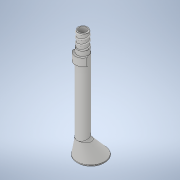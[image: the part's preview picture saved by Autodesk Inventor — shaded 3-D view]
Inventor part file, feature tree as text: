
AUTODESK INVENTOR PART (.ipt)
format: ipt  version: 2020 (Build 240168000, 168)  size: 341,504 bytes
history: native  units: mm
features: sketch x11, extrude x7, plane x5, fillet x4, other x3, loft x2, projected_geometry x1
ambient origin geometry x8: Origin, YZ Plane, XZ Plane, XY Plane, X Axis, Y Axis, Z Axis, Center Point
bodies: Volumenkörper1 (feature_tree)
feature tree (33):
  extrude  "Hals"  Depth=8.4mm
  extrude  "Ausschnitt Gewinde"  Depth=12.4mm
  other  "Grundfläche Gewinde"
  other  "Spirale nach oben"
  other  "Spirale nach unten"
  extrude  "Abschnitt oben"  Depth=16.0mm TaperAngle=0.0deg
  fillet  "Rundung1"  Radius=0.9mm
  plane  "Arbeitsebene4"
  plane  "Arbeitsebene5"
  plane  "Arbeitsebene6"
  loft  "Erhebung Gesamtkörper"
  loft  "Erhebung Ausschnitt"
  extrude  "Verbindung nach unten"  Depth=30.0mm
  extrude  "Nut unten"  TaperAngle=0.0deg  [1 undecoded]
  fillet  "Rundung5"  Radius=8.4mm
  fillet  "Rundung6"  Radius=26.0mm
  plane  "Arbeitsebene7"
  extrude  "Halterung"  TaperAngle=0.0deg  [1 undecoded]
  extrude  "Dünnerer Hals"  Depth=2.0mm
  fillet  "Rundung Halterung"  Radius=2.0mm
  sketch  "Skizze1"  dims[d0=12.4mm d1=8.4mm]
  sketch  "Skizze2"  dims[d2=49.0mm d3=52.0mm d4=0.0mm d5=0.0mm d6=12.4mm]
  sketch  "Skizze4"  dims[d7=1.0mm d8=16.0mm d9=0.0mm d10=0.9mm]
  plane  "Arbeitsebene3"
  sketch  "Skizze12"  dims[d11=5.0mm d12=10.0mm d13=45.0mm d14=0.0mm d15=90.0deg d16=90.0deg d17=0.0mm d18=0.0mm]
  sketch  "Skizze13"  dims[d19=5.0mm d20=10.0mm d21=10.0mm d22=0.0mm d23=90.0deg d24=90.0deg d25=0.0mm d26=0.0mm d27=14.0mm]
  sketch  "Skizze14"  dims[d28=10.0mm d29=0.0mm d30=0.2mm]
  sketch  "Skizze15"  dims[d60=-52.0mm d61=-20.0mm d72=30.0mm]
  sketch  "Skizze16"  dims[d73=12.4mm d74=0.0mm d75=90.0deg d76=0.0mm d77=90.0deg d78=8.4mm d79=26.0mm]
  sketch  "Skizze17"  dims[d80=0.0mm d81=90.0deg d82=0.0mm d83=90.0deg]
  sketch  "Skizze19"  dims[d84=30.0mm d85=26.0mm d86=2.0mm d87=0.0mm]
  projected_geometry  "Projizierte Kontur1"
  sketch  "Skizze20"  dims[d90=30.0mm d92=1.1mm d93=1.1mm d94=0.0mm d95=1.0mm d96=9.25mm d98=-21.0mm d99=10.0mm d100=0.0mm d101=12.0mm d102=12.4mm d103=5.0mm d104=0.0mm d105=2.0mm]
note: 2 required parameter values undecoded (feature->parameter linkage not recoverable at this tier; creation-order binding heuristic only, values carry confidence <= 0.55)
